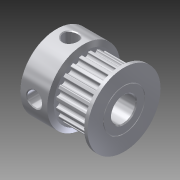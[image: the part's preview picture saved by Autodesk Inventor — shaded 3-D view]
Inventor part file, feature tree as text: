
AUTODESK INVENTOR PART (.ipt)
format: ipt  version: 2015 SP1 (Build 190203100, 203)  size: 442,368 bytes
history: native  units: in
note: dims shown in document units (in); Inventor stores cm internally (conversion verified against a paired STEP export)
features: other x2, plane x1, imported_body x1
ambient origin geometry x8: Origin, YZ Plane, XZ Plane, XY Plane, X Axis, Y Axis, Z Axis, Center Point
bodies: Body1 (feature_tree)
feature tree (4):
  other  "Круговой массив1"
  other  "GT2_20tooth1"
  plane  "Work Plane1"
  imported_body  "Base1"
